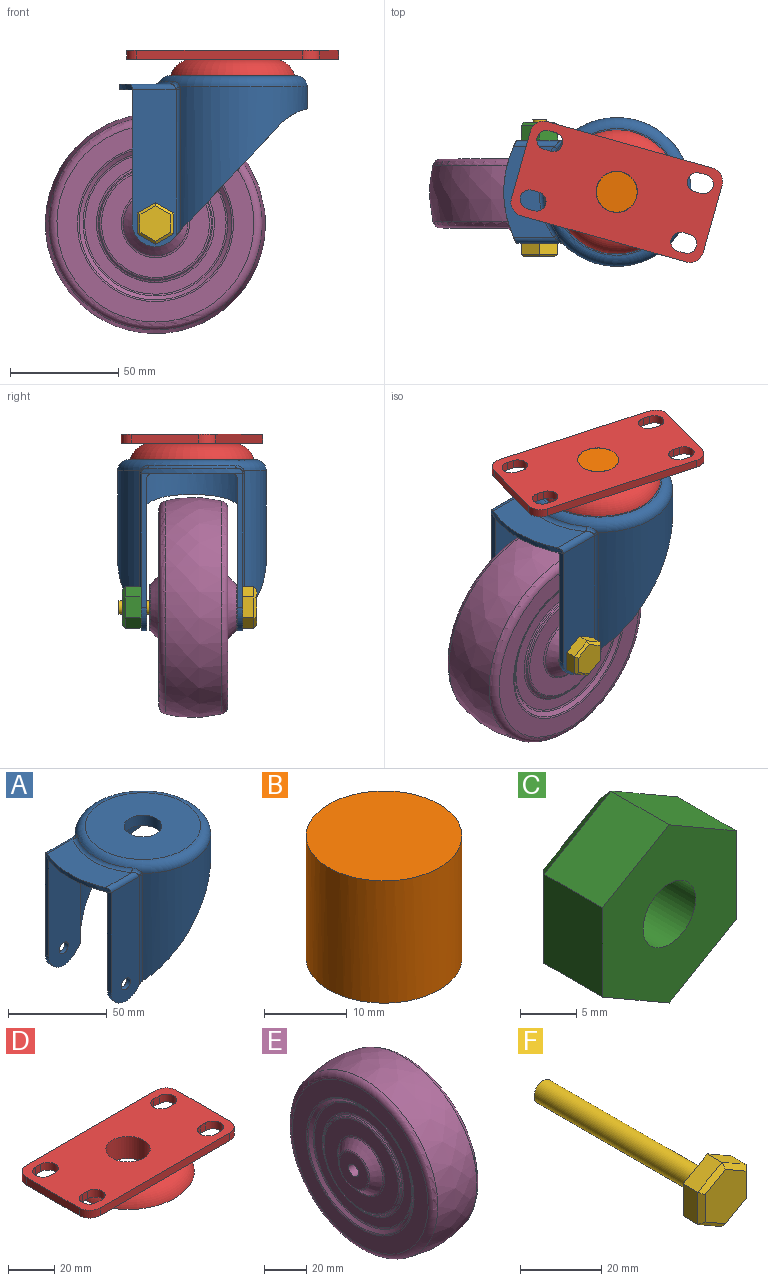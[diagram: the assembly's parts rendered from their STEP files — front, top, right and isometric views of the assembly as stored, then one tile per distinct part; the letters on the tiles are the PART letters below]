
ASSEMBLY  parts=6 mates=5
PART A: 32 faces, bbox 89.3x74.4x78.9 mm
  f0: plane 52.93x49.61mm, normal (0.73,0,-0.68), area 202.5mm2, adj f5,f7,f9,f12,f14,f16,f24
  f1: cylinder r=10.67mm len=18.45mm, axis (0,-1,0), area 64.7mm2, adj f2,f4,f8,f15
  f2: plane 61.72x5.08mm, normal (-1,0,0), area 158.2mm2, adj f1,f4,f11,f15,f21
  f3: plane 41.91x23.03mm, normal (0,0,1), area 710.2mm2, adj f6,f22,f23,f27
  f4: plane 72.39x20.26mm, normal (0,-1,0), area 1392mm2, adj f1,f2,f8,f17,f23,f30
  f5: plane 72.39x20.26mm, normal (0,1,0), area 1392mm2, adj f0,f9,f10,f18,f22,f24
  f6: cylinder r=50.8mm len=46.99mm, axis (0,0,1), area 121mm2, adj f3,f11,f22,f23
  f7: cylinder r=34.29mm len=68.58mm, axis (0,0,1), area 4988.6mm2, adj f0,f8,f12,f19,f24,f25,f29,f30
  f8: plane 52.93x49.61mm, normal (0.73,0,-0.68), area 202.5mm2, adj f1,f4,f7,f12,f15,f16,f30
  f9: cylinder r=10.67mm len=18.45mm, axis (0,-1,0), area 64.7mm2, adj f0,f5,f10,f14
  f10: plane 61.72x5.08mm, normal (-1,0,0), area 158.2mm2, adj f5,f9,f11,f14,f20
  f11: plane 83.82x63.5mm, normal (0,0,-1), area 3670.1mm2, adj f2,f6,f10,f16,f20,f21,f31
  f12: cylinder r=25.4mm len=53.28mm, axis (0,-1,0), area 163.5mm2, adj f0,f7,f8,f16
  f13: plane 58.42x58.42mm, normal (0,0,1), area 2395.5mm2, adj f19,f31
  f14: plane 69.85x22.46mm, normal (0,-1,0), area 1479.8mm2, adj f0,f9,f10,f16,f18,f20
  f15: plane 69.85x22.46mm, normal (0,1,0), area 1479.8mm2, adj f1,f2,f8,f16,f17,f21
  f16: cylinder r=31.75mm len=64.74mm, axis (0,0,1), area 4743.9mm2, adj f0,f8,f11,f12,f14,f15,f20,f21
  f17: cylinder r=3.3mm len=6.6mm, axis (0,-1,0), area 52.7mm2, adj f4,f15
  f18: cylinder r=3.3mm len=6.6mm, axis (0,-1,0), area 52.7mm2, adj f5,f14
  f19: torus R=29.21mm, axis (0,0,1), area 1492.8mm2, adj f7,f13,f26,f27,f28
  f20: cylinder r=2.54mm len=22.46mm, axis (-1,0,0), area 86.6mm2, adj f10,f11,f14,f16
  f21: cylinder r=2.54mm len=22.46mm, axis (1,0,0), area 86.6mm2, adj f2,f11,f15,f16
  f22: cylinder r=2.54mm len=21.5mm, axis (-1,0,0), area 78.3mm2, adj f3,f5,f6,f25,f26
  f23: cylinder r=2.54mm len=21.5mm, axis (1,0,0), area 78.3mm2, adj f3,f4,f6,f28,f29
  f24: cylinder r=2.54mm len=67.09mm, axis (0,0,1), area 132mm2, adj f0,f5,f7,f25
  f25: bspline ~3.18x2.31mm, area 1.9mm2, adj f7,f22,f24,f26
  f26: bspline ~5.4x5.25mm, area 11.3mm2, adj f19,f22,f25,f27
  f27: torus R=35.81mm, axis (0,0,1), area 115mm2, adj f3,f19,f26,f28
  f28: bspline ~5.4x5.25mm, area 11.3mm2, adj f19,f23,f27,f29
  f29: bspline ~2.45x2.03mm, area 1.9mm2, adj f7,f23,f28,f30
  f30: cylinder r=2.54mm len=67.09mm, axis (0,0,1), area 132mm2, adj f4,f7,f8,f29
  f31: cylinder r=9.53mm len=19.05mm, axis (0,0,-1), area 380mm2, adj f11,f13
PART B: 3 faces, bbox 18.8x18.8x18 mm
  f0: plane 18.8x18.8mm, normal (0,0,-1), area 277.5mm2, adj f2
  f1: plane 18.8x18.8mm, normal (0,0,1), area 277.5mm2, adj f2
  f2: cylinder r=9.4mm len=18.8mm, axis (0,0,1), area 1064.9mm2, adj f0,f1
PART C: 15 faces, bbox 16.8x8.6x19.4 mm
  f0: plane 9.68x7.37mm, normal (1,0,0), area 71.3mm2, adj f1,f5,f8,f11
  f1: plane 8.38x7.37mm, normal (0.5,0,-0.87), area 71.3mm2, adj f0,f2,f8,f13
  f2: plane 8.38x7.37mm, normal (-0.5,0,-0.87), area 71.3mm2, adj f1,f3,f8,f14
  f3: plane 9.68x7.37mm, normal (-1,0,0), area 71.3mm2, adj f2,f4,f8,f12
  f4: plane 8.38x7.37mm, normal (-0.5,0,0.87), area 71.3mm2, adj f3,f5,f8,f10
  f5: plane 8.38x7.37mm, normal (0.5,0,0.87), area 71.3mm2, adj f0,f4,f8,f9
  f6: cylinder r=3.3mm len=8.64mm, axis (0,-1,0), area 179.2mm2, adj f7,f8
  f7: plane 16.42x14.22mm, normal (0,1,0), area 141mm2, adj f6,f9,f10,f11,f12,f13,f14
  f8: plane 19.36x16.76mm, normal (0,-1,0), area 209.1mm2, adj f0,f1,f2,f3,f4,f5,f6
  f9: plane 8.38x5.57mm, normal (0.35,0.71,0.61), area 16.1mm2, adj f5,f7,f10,f11
  f10: plane 8.38x5.57mm, normal (-0.35,0.71,0.61), area 16.1mm2, adj f4,f7,f9,f12
  f11: plane 9.68x1.27mm, normal (0.71,0.71,0), area 16.1mm2, adj f0,f7,f9,f13
  f12: plane 9.68x1.27mm, normal (-0.71,0.71,0), area 16.1mm2, adj f3,f7,f10,f14
  f13: plane 8.38x5.57mm, normal (0.35,0.71,-0.61), area 16.1mm2, adj f1,f7,f11,f14
  f14: plane 8.38x5.57mm, normal (-0.35,0.71,-0.61), area 16.1mm2, adj f2,f7,f12,f13
PART D: 29 faces, bbox 91.8x62.6x14.2 mm
  f0: plane 4.06x3.18mm, normal (0,1,0), area 12.9mm2, adj f1,f23,f24,f25
  f1: cylinder r=4.45mm len=8.89mm, axis (0,0,-1), area 56.8mm2, adj f0,f2,f24,f25
  f2: plane 4.06x3.18mm, normal (0,-1,0), area 12.9mm2, adj f1,f23,f24,f25
  f3: plane 4.06x3.18mm, normal (0,-1,0), area 12.9mm2, adj f4,f19,f24,f25
  f4: cylinder r=4.45mm len=8.89mm, axis (0,0,-1), area 56.8mm2, adj f3,f5,f24,f25
  f5: plane 4.06x3.18mm, normal (0,1,0), area 12.9mm2, adj f4,f19,f24,f25
  f6: cylinder r=6.35mm len=6.35mm, axis (0,0,-1), area 40.5mm2, adj f7,f20,f24,f25
  f7: plane 79.12x4.06mm, normal (0,-1,0), area 321.5mm2, adj f6,f8,f24,f25
  f8: cylinder r=6.35mm len=6.35mm, axis (0,0,-1), area 40.5mm2, adj f7,f9,f24,f25
  f9: plane 32.3x4.06mm, normal (1,0,0), area 131.3mm2, adj f8,f10,f24,f25
  f10: cylinder r=6.35mm len=6.35mm, axis (0,0,-1), area 40.5mm2, adj f9,f11,f24,f25
  f11: plane 79.12x4.06mm, normal (0,1,0), area 321.5mm2, adj f10,f12,f24,f25
  f12: cylinder r=6.35mm len=6.35mm, axis (0,0,-1), area 40.5mm2, adj f11,f20,f24,f25
  f13: plane 4.06x3.18mm, normal (0,-1,0), area 12.9mm2, adj f14,f21,f24,f25
  f14: cylinder r=4.45mm len=8.89mm, axis (0,0,-1), area 56.8mm2, adj f13,f15,f24,f25
  f15: plane 4.06x3.18mm, normal (0,1,0), area 12.9mm2, adj f14,f21,f24,f25
  f16: cylinder r=4.45mm len=8.89mm, axis (0,0,-1), area 56.8mm2, adj f17,f22,f24,f25
  f17: plane 4.06x3.18mm, normal (0,1,0), area 12.9mm2, adj f16,f18,f24,f25
  f18: cylinder r=4.45mm len=8.89mm, axis (0,0,-1), area 56.8mm2, adj f17,f22,f24,f25
  f19: cylinder r=4.45mm len=8.89mm, axis (0,0,-1), area 56.8mm2, adj f3,f5,f24,f25
  f20: plane 32.3x4.06mm, normal (-1,0,0), area 131.3mm2, adj f6,f12,f24,f25
  f21: cylinder r=4.45mm len=8.89mm, axis (0,0,-1), area 56.8mm2, adj f13,f15,f24,f25
  f22: plane 4.06x3.18mm, normal (0,-1,0), area 12.9mm2, adj f16,f18,f24,f25
  f23: cylinder r=4.45mm len=8.89mm, axis (0,0,-1), area 56.8mm2, adj f0,f2,f24,f25
  f24: plane 91.82x45mm, normal (0,0,1), area 3451.1mm2, adj f0,f1,f2,f3,f4,f5,f6,f7
  f25: plane 91.82x45mm, normal (0,0,-1), area 2633.1mm2, adj f0,f1,f2,f3,f4,f5,f6,f7
  f26: plane 57.15x57.15mm, normal (0,0,-1), area 2280.2mm2, adj f27,f28
  f27: torus R=18.74mm, axis (0,0,1), area 2063.1mm2, adj f25,f26
  f28: cylinder r=9.53mm len=19.05mm, axis (0,0,1), area 699.3mm2, adj f24,f26
PART E: 30 faces, bbox 40.6x106.6x106.6 mm
  f0: revolved ~101.6x101.6mm, area 16650.5mm2, adj f16,f17
  f1: plane 90.84x90.84mm, normal (-1,0,0), area 2412.6mm2, adj f16,f18
  f2: cone r=35.56mm half-angle=53.1deg, axis (-1,0,0), area 501.6mm2, adj f18,f19
  f3: plane 65.19x65.19mm, normal (-1,0,0), area 1014.5mm2, adj f19,f20
  f4: cone r=26.67mm half-angle=45deg, axis (1,0,0), area 121.7mm2, adj f20,f21
  f5: plane 49.75x49.75mm, normal (-1,0,0), area 1162.8mm2, adj f21,f22
  f6: cone r=15.24mm half-angle=45deg, axis (1,0,0), area 489.3mm2, adj f22,f23
  f7: plane 19.27x19.27mm, normal (-1,0,0), area 257.3mm2, adj f15,f23
  f8: plane 19.27x19.27mm, normal (1,0,0), area 257.3mm2, adj f15,f24
  f9: cone r=15.24mm half-angle=45deg, axis (-1,0,0), area 489.3mm2, adj f24,f25
  f10: plane 49.75x49.75mm, normal (1,0,0), area 1162.8mm2, adj f25,f26
  f11: cone r=26.67mm half-angle=45deg, axis (-1,0,0), area 121.7mm2, adj f26,f27
  f12: plane 65.19x65.19mm, normal (1,0,0), area 1014.5mm2, adj f27,f28
  f13: cone r=35.56mm half-angle=53.1deg, axis (1,0,0), area 501.6mm2, adj f28,f29
  f14: plane 90.84x90.84mm, normal (1,0,0), area 2412.6mm2, adj f17,f29
  f15: cylinder r=3.3mm len=40.64mm, axis (-1,0,0), area 843.2mm2, adj f7,f8
  f16: torus R=45.42mm, axis (-1,0,0), area 1493.8mm2, adj f0,f1
  f17: torus R=45.42mm, axis (-1,0,0), area 1493.8mm2, adj f0,f14
  f18: torus R=35.98mm, axis (-1,0,0), area 182.7mm2, adj f1,f2
  f19: torus R=32.6mm, axis (-1,0,0), area 169.4mm2, adj f2,f3
  f20: torus R=27.2mm, axis (-1,0,0), area 167.5mm2, adj f3,f4
  f21: torus R=24.87mm, axis (-1,0,0), area 158.9mm2, adj f4,f5
  f22: torus R=15.77mm, axis (-1,0,0), area 95.8mm2, adj f5,f6
  f23: torus R=9.63mm, axis (-1,0,0), area 63.3mm2, adj f6,f7
  f24: torus R=9.63mm, axis (-1,0,0), area 63.3mm2, adj f8,f9
  f25: torus R=15.77mm, axis (-1,0,0), area 95.8mm2, adj f9,f10
  f26: torus R=24.87mm, axis (-1,0,0), area 158.9mm2, adj f10,f11
  f27: torus R=27.2mm, axis (-1,0,0), area 167.5mm2, adj f11,f12
  f28: torus R=32.6mm, axis (-1,0,0), area 169.4mm2, adj f12,f13
  f29: torus R=35.98mm, axis (-1,0,0), area 182.7mm2, adj f13,f14
PART F: 16 faces, bbox 16.8x63.5x19.4 mm
  f0: plane 9.68x5.08mm, normal (-1,0,0), area 49.2mm2, adj f1,f5,f7,f10
  f1: plane 8.38x5.08mm, normal (-0.5,0,-0.87), area 49.2mm2, adj f0,f2,f7,f12
  f2: plane 8.38x5.08mm, normal (0.5,0,-0.87), area 49.2mm2, adj f1,f3,f7,f14
  f3: plane 9.68x5.08mm, normal (1,0,0), area 49.2mm2, adj f2,f4,f7,f15
  f4: plane 8.38x5.08mm, normal (0.5,0,0.87), area 49.2mm2, adj f3,f5,f7,f13
  f5: plane 8.38x5.08mm, normal (-0.5,0,0.87), area 49.2mm2, adj f0,f4,f7,f11
  f6: plane 16.42x14.22mm, normal (0,-1,0), area 175.2mm2, adj f10,f11,f12,f13,f14,f15
  f7: plane 19.36x16.76mm, normal (0,1,0), area 211.7mm2, adj f0,f1,f2,f3,f4,f5,f8
  f8: cylinder r=3.17mm len=57.15mm, axis (0,-1,0), area 1140.1mm2, adj f7,f9
  f9: plane 6.35x6.35mm, normal (0,1,0), area 31.7mm2, adj f8
  f10: plane 9.68x1.27mm, normal (-0.71,-0.71,0), area 16.1mm2, adj f0,f6,f11,f12
  f11: plane 8.38x5.57mm, normal (-0.35,-0.71,0.61), area 16.1mm2, adj f5,f6,f10,f13
  f12: plane 8.38x5.57mm, normal (-0.35,-0.71,-0.61), area 16.1mm2, adj f1,f6,f10,f14
  f13: plane 8.38x5.57mm, normal (0.35,-0.71,0.61), area 16.1mm2, adj f4,f6,f11,f15
  f14: plane 8.38x5.57mm, normal (0.35,-0.71,-0.61), area 16.1mm2, adj f2,f6,f12,f15
  f15: plane 9.68x1.27mm, normal (0.71,-0.71,0), area 16.1mm2, adj f3,f6,f13,f14
PLACE A t=(2.14,-18.41,23.25)mm fixed
PLACE B t=(2.14,-18.41,37.22)mm
PLACE C t=(2.14,-18.41,23.25)mm
PLACE D rot(axis=(0,0,1),164.3deg) t=(2.14,-18.41,37.22)mm
PLACE E rot(axis=(-0.63,-0.63,0.45),131.7deg) t=(-33.5,-19.04,-38.47)mm
PLACE F t=(2.14,-18.41,23.25)mm
MATE fastened C.f6 <-> A.f1  axis (0,-1,0) through (-33.5,5.09,-38.47)mm
MATE cylindrical E.f2 <-> A.f1  axis (0,-1,0) through (-33.5,-39.36,-38.47)mm
MATE fastened A.f31 <-> B.f2  axis (0,0,-1) through (2.14,-18.41,23.25)mm
MATE revolute D.f28 <-> B.f2  axis (0,0,1) through (2.14,-18.41,41.28)mm
MATE fastened A.f1 <-> F.f8  axis (0,-1,0) through (-33.5,-41.9,-38.47)mm
